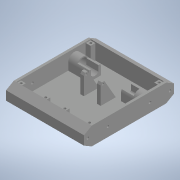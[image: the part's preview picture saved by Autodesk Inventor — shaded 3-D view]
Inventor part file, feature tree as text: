
AUTODESK INVENTOR PART (.ipt)
format: ipt  version: 2020 (Build 240168000, 168)  size: 391,680 bytes
history: native  units: in
note: dims shown in document units (in); Inventor stores cm internally (conversion verified against a paired STEP export)
features: projected_geometry x13, extrude x11, sketch x11, mirror x4, plane x1
ambient origin geometry x8: Origin, YZ Plane, XZ Plane, XY Plane, X Axis, Y Axis, Z Axis, Center Point
bodies: Solid1 (feature_tree)
feature tree (40):
  extrude  "Extrusion1"  Depth=5.9055in
  extrude  "Extrusion2"  TaperAngle=0.0deg  [1 undecoded]
  extrude  "Extrusion3"  Depth=1.063in
  extrude  "Extrusion4"  Depth=0.315in
  extrude  "Extrusion5"  TaperAngle=0.0deg  [1 undecoded]
  extrude  "Extrusion6"  Depth=0.5906in
  mirror  "Mirror1"
  extrude  "Extrusion7"  Depth=0.0787in
  mirror  "Mirror2"
  extrude  "Extrusion8"  Depth=0.5512in
  mirror  "Mirror3"
  plane  "Work Plane1"
  extrude  "Extrusion9"  Depth=0.7874in TaperAngle=0.0deg
  mirror  "Mirror4"
  extrude  "Extrusion10"  Depth=6.063in TaperAngle=0.0deg
  extrude  "Extrusion11"  Depth=0.1575in
  sketch  "Sketch1"  dims[d0=1.1811in d1=5.9055in]
  sketch  "Sketch2"  dims[d2=5.1181in d3=0.0in]
  projected_geometry  "Projected Loop1"
  sketch  "Sketch3"  dims[d4=0.1575in d5=1.063in]
  projected_geometry  "Projected Loop2"
  projected_geometry  "Projected Loop3"
  sketch  "Sketch4"  dims[d6=0.0in d8=0.315in]
  sketch  "Sketch5"  dims[d10=0.993in d11=0.0in]
  projected_geometry  "Projected Loop4"
  sketch  "Sketch6"  dims[d12=0.6496in d13=0.5906in]
  sketch  "Sketch7"  dims[d14=1.5748in d15=0.0787in]
  sketch  "Sketch9"  dims[d16=0.5512in d17=0.0in d18=0.6102in]
  sketch  "Sketch10"  dims[d19=0.4803in d20=0.7874in d21=0.0in]
  sketch  "Sketch12"  dims[d22=0.1654in d23=6.063in d24=0.0in]
  projected_geometry  "Projected Loop6"
  projected_geometry  "Projected Loop7"
  projected_geometry  "Projected Loop8"
  sketch  "Sketch13"  dims[d25=0.5114in d26=0.1575in d27=1.5748in d28=0.0in d29=0.0in d30=0.1575in d31=0.2756in d32=0.0in d33=0.4331in d34=0.122in d38=2.7559in d40=0.061in d41=0.0909in d42=0.2362in d43=0.0in d44=60.0deg d45=0.0787in d46=0.315in d48=0.993in d49=0.0in d51=0.1575in d52=0.1575in d53=0.2756in d54=0.0in d55=0.4724in]
  projected_geometry  "Projected Loop9"
  projected_geometry  "Projected Loop10"
  projected_geometry  "Projected Loop11"
  projected_geometry  "Projected Loop12"
  projected_geometry  "Projected Loop13"
  projected_geometry  "Projected Loop14"
note: 2 required parameter values undecoded (feature->parameter linkage not recoverable at this tier; creation-order binding heuristic only, values carry confidence <= 0.55)
